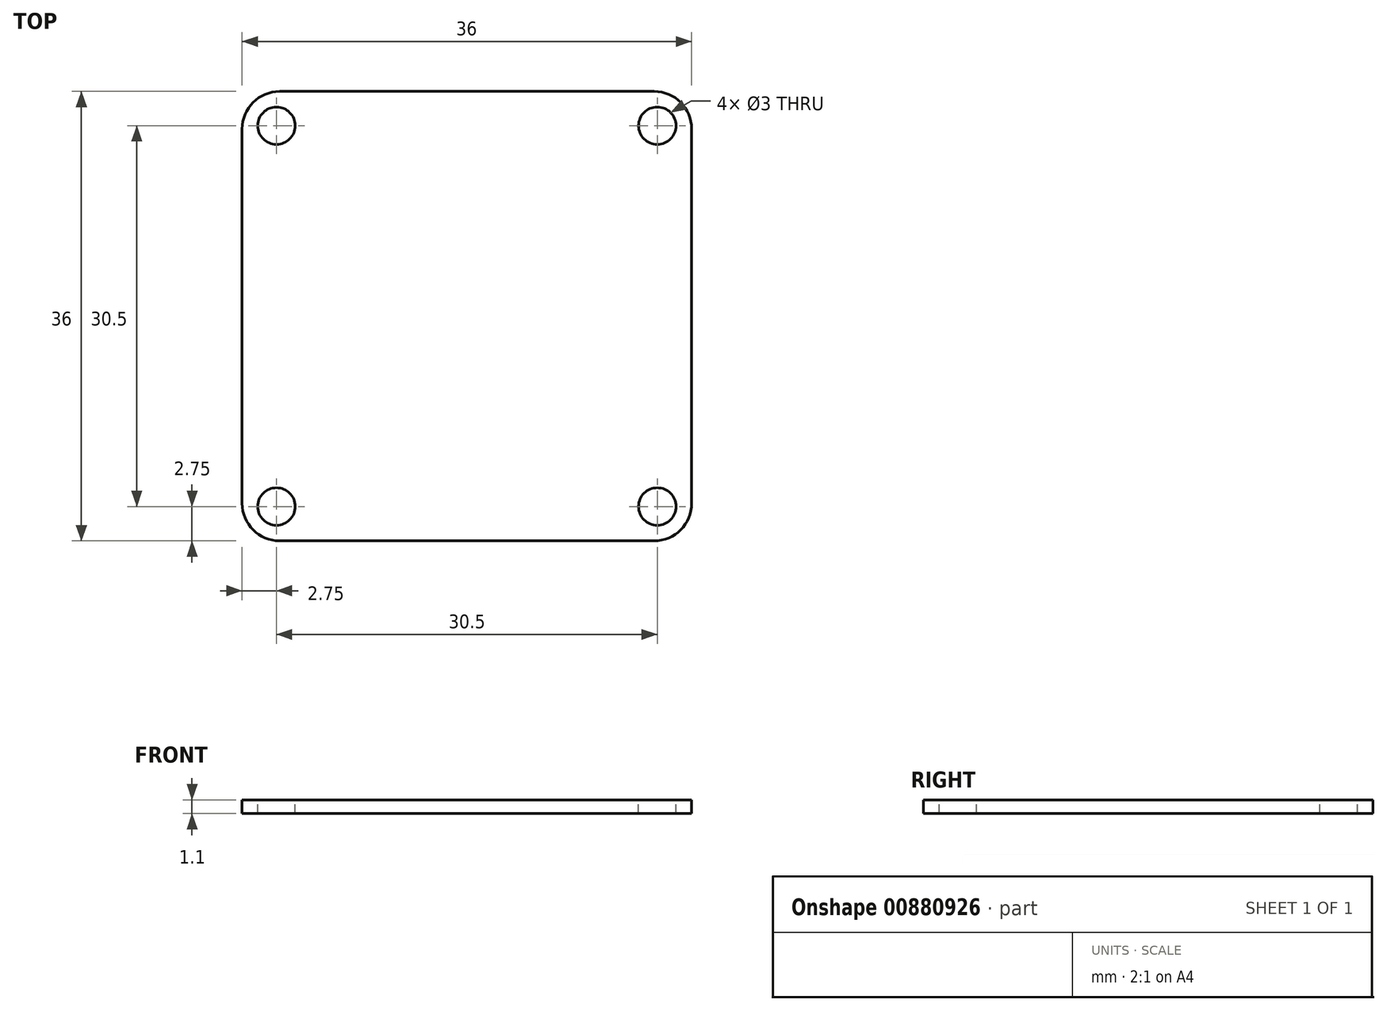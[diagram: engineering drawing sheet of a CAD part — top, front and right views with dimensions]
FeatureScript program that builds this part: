
annotation { "Feature Type Name" : "Feature", "Feature Type Description" : "" }
export const myFeature = defineFeature(function(context is Context, id is Id, definition is map)
    precondition{}
    {
        {
            var Q0;
            Q0=qCreatedBy(makeId("Top.planeOp"),FACE);
            var sketch = newSketch(context, id + "F0", { "sketchPlane" : qUnion([Q0])});
            skLineSegment(sketch, "E0.bottom", {"start": v(0, 0) * mm, "end": v(36, 0) * mm});
            skLineSegment(sketch, "E0.top", {"start": v(0, 36) * mm, "end": v(36, 36) * mm});
            skLineSegment(sketch, "E0.left", {"start": v(0, 0) * mm, "end": v(0, 36) * mm});
            skLineSegment(sketch, "E0.right", {"start": v(36, 0) * mm, "end": v(36, 36) * mm});
            skSolve(sketch);
        }
        {
            var Q0;
            Q0=makeQuery(id+"F0.imprint","IMPRINT",FACE,{"disambiguationData":[TD([[makeQuery(id+"F0.imprint","IMPRINT",EDGE,{"derivedFrom":sQuery(id+"F0.wireOp",EDGE,"E0.bottom")}),1.0]])]});
            extrude(context, id + "F1", {"entities" : qUnion([Q0]), "depth" : 1.1 * mm, "offsetDistance" : 25 * mm});
        }
        {
            var Q0;
            Q0=makeQuery(id+"F1.opExtrude","CAP_FACE",FACE,{"disambiguationData":[OSD([sQuery(id+"F0.wireOp",EDGE,"E0.bottom"),sQuery(id+"F0.wireOp",EDGE,"E0.top"),sQuery(id+"F0.wireOp",EDGE,"E0.left"),sQuery(id+"F0.wireOp",EDGE,"E0.right")])],"isStart":false});
            var sketch = newSketch(context, id + "F2", { "sketchPlane" : qUnion([Q0])});
            skLineSegment(sketch, "E1.0.0", {"start": v(36, 36) * mm, "end": v(0, 36) * mm});
            skLineSegment(sketch, "E1.0.1", {"start": v(0, 36) * mm, "end": v(0, 0) * mm});
            skLineSegment(sketch, "E1.0.2", {"start": v(0, 0) * mm, "end": v(36, 0) * mm});
            skLineSegment(sketch, "E1.0.3", {"start": v(36, 0) * mm, "end": v(36, 36) * mm});
            skLineSegment(sketch, "E2.bottom", {"start": v(2.75, 33.25) * mm, "end": v(33.25, 33.25) * mm});
            skLineSegment(sketch, "E2.top", {"start": v(2.75, 2.75) * mm, "end": v(33.25, 2.75) * mm});
            skLineSegment(sketch, "E2.left", {"start": v(2.75, 33.25) * mm, "end": v(2.75, 2.75) * mm});
            skLineSegment(sketch, "E2.right", {"start": v(33.25, 33.25) * mm, "end": v(33.25, 2.75) * mm});
            skLineSegment(sketch, "E3", {"start": v(18, 36) * mm, "end": v(18, 33.25) * mm});
            skLineSegment(sketch, "E4", {"start": v(33.25, 18) * mm, "end": v(36, 18) * mm});
            skSolve(sketch);
        }
        {
            var Q0;
            Q0=sQuery(id+"F2.wireOp",VERTEX,"E2.bottom.start");
            var Q1;
            Q1=sQuery(id+"F2.wireOp",VERTEX,"E2.bottom.end");
            var Q2;
            Q2=sQuery(id+"F2.wireOp",VERTEX,"E2.top.start");
            var Q3;
            Q3=sQuery(id+"F2.wireOp",VERTEX,"E2.top.end");
            var Q4;
            Q4=makeQuery(id+"F1.opExtrude","SWEPT_BODY",BODY,{"disambiguationData":[OSD([sQuery(id+"F0.wireOp",EDGE,"E0.bottom"),sQuery(id+"F0.wireOp",EDGE,"E0.top"),sQuery(id+"F0.wireOp",EDGE,"E0.left"),sQuery(id+"F0.wireOp",EDGE,"E0.right")])]});
            hole(context, id + "F3", {"style" : HoleStyle.SIMPLE, "endStyle" : HoleEndStyle.THROUGH, "standardTappedOrClearance" : lookupTablePath({ "standard" : "ISO", "size" : "3", "type" : "Drilled" }), "standardBlindInLast" : lookupTablePath({ "standard" : "ISO", "size" : "3", "type" : "Drilled" }), "holeDiameter" : 3 * mm, "majorDiameter" : 3 * mm, "isTappedThrough" : true, "tappedDepth" : 12 * mm, "tapClearance" : 3, "locations" : qUnion([Q0, Q1, Q2, Q3]), "scope" : qUnion([Q4])});
        }
        {
            var Q0;
            Q0=makeQuery(id+"F1.opExtrude","SWEPT_EDGE",EDGE,{"disambiguationData":[OSD([sQuery(id+"F0.wireOp",EDGE,"E0.bottom"),sQuery(id+"F0.wireOp",EDGE,"E0.right")])]});
            var Q1;
            Q1=makeQuery(id+"F1.opExtrude","SWEPT_EDGE",EDGE,{"disambiguationData":[OSD([sQuery(id+"F0.wireOp",EDGE,"E0.bottom"),sQuery(id+"F0.wireOp",EDGE,"E0.left")])]});
            var Q2;
            Q2=makeQuery(id+"F1.opExtrude","SWEPT_EDGE",EDGE,{"disambiguationData":[OSD([sQuery(id+"F0.wireOp",EDGE,"E0.top"),sQuery(id+"F0.wireOp",EDGE,"E0.left")])]});
            var Q3;
            Q3=makeQuery(id+"F1.opExtrude","SWEPT_EDGE",EDGE,{"disambiguationData":[OSD([sQuery(id+"F0.wireOp",EDGE,"E0.top"),sQuery(id+"F0.wireOp",EDGE,"E0.right")])]});
            fillet(context, id + "F4", {"entities" : qUnion([Q0, Q1, Q2, Q3]), "radius" : 3 * mm, "tangentPropagation" : true, "allowEdgeOverflow" : false});
        }
    });
